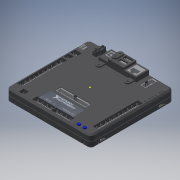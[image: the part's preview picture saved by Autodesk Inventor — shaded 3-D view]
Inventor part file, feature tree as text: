
AUTODESK INVENTOR PART (.ipt)
format: ipt  version: 2017 SP1 (Build 210196100, 196)  size: 38,966,272 bytes
history: native  units: in
note: dims shown in document units (in); Inventor stores cm internally (conversion verified against a paired STEP export)
features: imported_body x16, other x3, sketch x2
ambient origin geometry x8: Origin, YZ Plane, XZ Plane, XY Plane, X Axis, Y Axis, Z Axis, Center Point
bodies: Solid1 (feature_tree), Solid2 (feature_tree), Solid3 (feature_tree), Solid4 (feature_tree), Solid5 (feature_tree), Solid6 (feature_tree), Solid7 (feature_tree), Solid8 (feature_tree), Solid9 (feature_tree), Solid10 (feature_tree), Solid11 (feature_tree), Solid12 (feature_tree), Solid13 (feature_tree), Solid14 (feature_tree), Solid15 (feature_tree), Solid16 (feature_tree)
feature tree (21):
  other  "cd_roborio1"
  sketch  "Sketch1"
  other  "Decal2"
  imported_body  "Base1"
  imported_body  "Base2"
  imported_body  "Base3"
  imported_body  "Base4"
  imported_body  "Base5"
  imported_body  "Base6"
  imported_body  "Base7"
  imported_body  "Base8"
  imported_body  "Base9"
  imported_body  "Base10"
  imported_body  "Base11"
  imported_body  "Base12"
  imported_body  "Base13"
  imported_body  "Base14"
  imported_body  "Base15"
  imported_body  "Base16"
  sketch  "Sketch3"
  other  "Image2"
